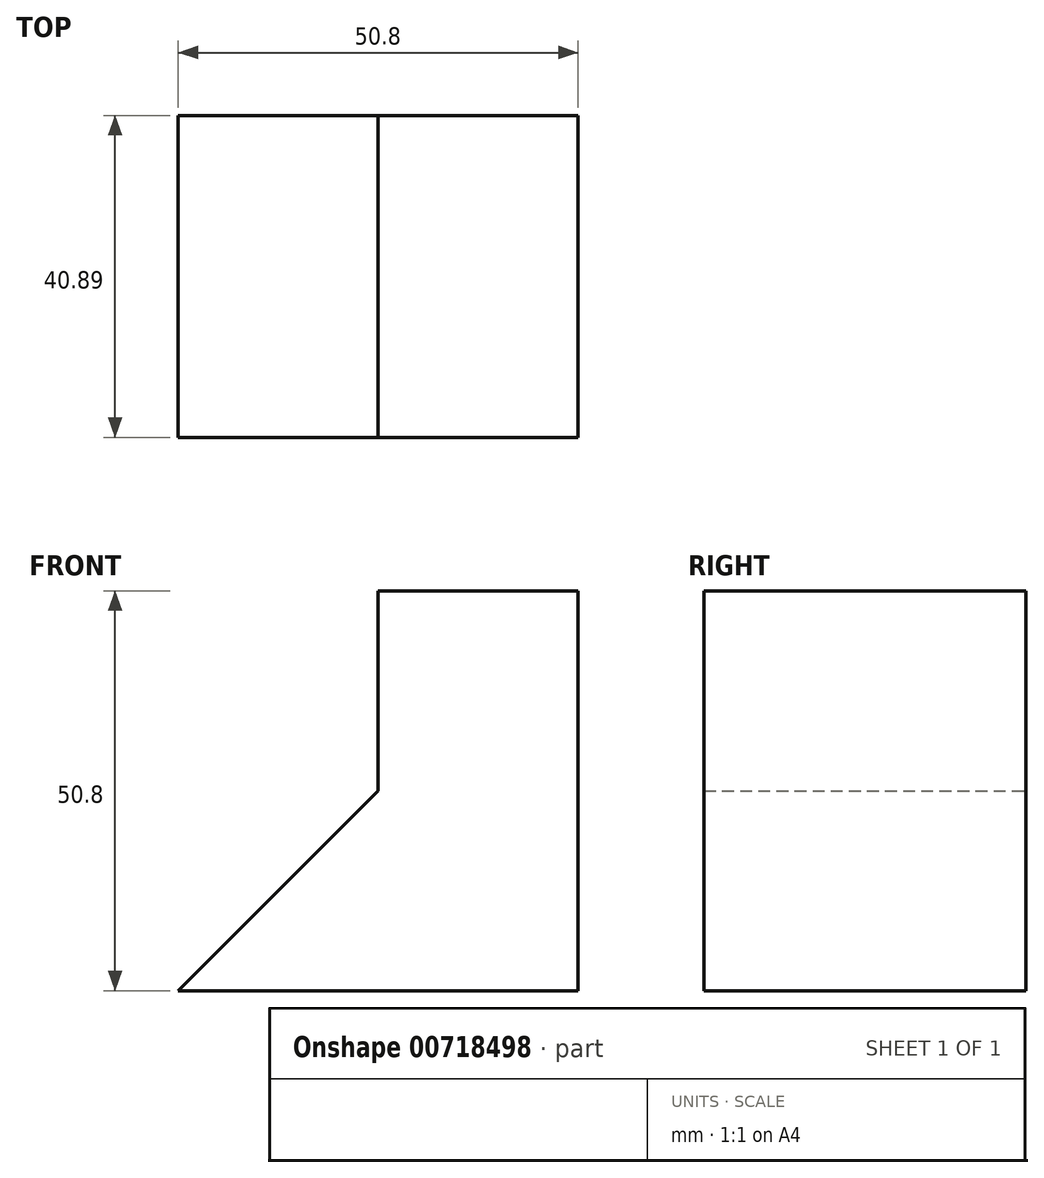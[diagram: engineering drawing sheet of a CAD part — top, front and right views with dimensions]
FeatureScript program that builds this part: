
annotation { "Feature Type Name" : "Feature", "Feature Type Description" : "" }
export const myFeature = defineFeature(function(context is Context, id is Id, definition is map)
    precondition{}
    {
        {
            var Q0;
            Q0=qCreatedBy(makeId("Front.planeOp"),FACE);
            var sketch = newSketch(context, id + "F0", { "sketchPlane" : qUnion([Q0])});
            skLineSegment(sketch, "E0", {"start": v(-49.18, 0) * mm, "end": v(1.62, 0) * mm});
            skLineSegment(sketch, "E1", {"start": v(1.62, 0) * mm, "end": v(1.62, 50.8) * mm});
            skLineSegment(sketch, "E2", {"start": v(1.62, 50.8) * mm, "end": v(-23.78, 50.8) * mm});
            skLineSegment(sketch, "E3", {"start": v(-23.78, 50.8) * mm, "end": v(-23.78, 25.4) * mm});
            skLineSegment(sketch, "E4", {"start": v(-23.78, 25.4) * mm, "end": v(-49.18, 0) * mm});
            skSolve(sketch);
        }
        {
            var Q0;
            Q0 = qSketchRegion(id + "F0", true);
            extrude(context, id + "F1", {"entities" : qUnion([Q0]), "depth" : 40.9 * mm, "offsetDistance" : 25.4 * mm});
        }
    });
